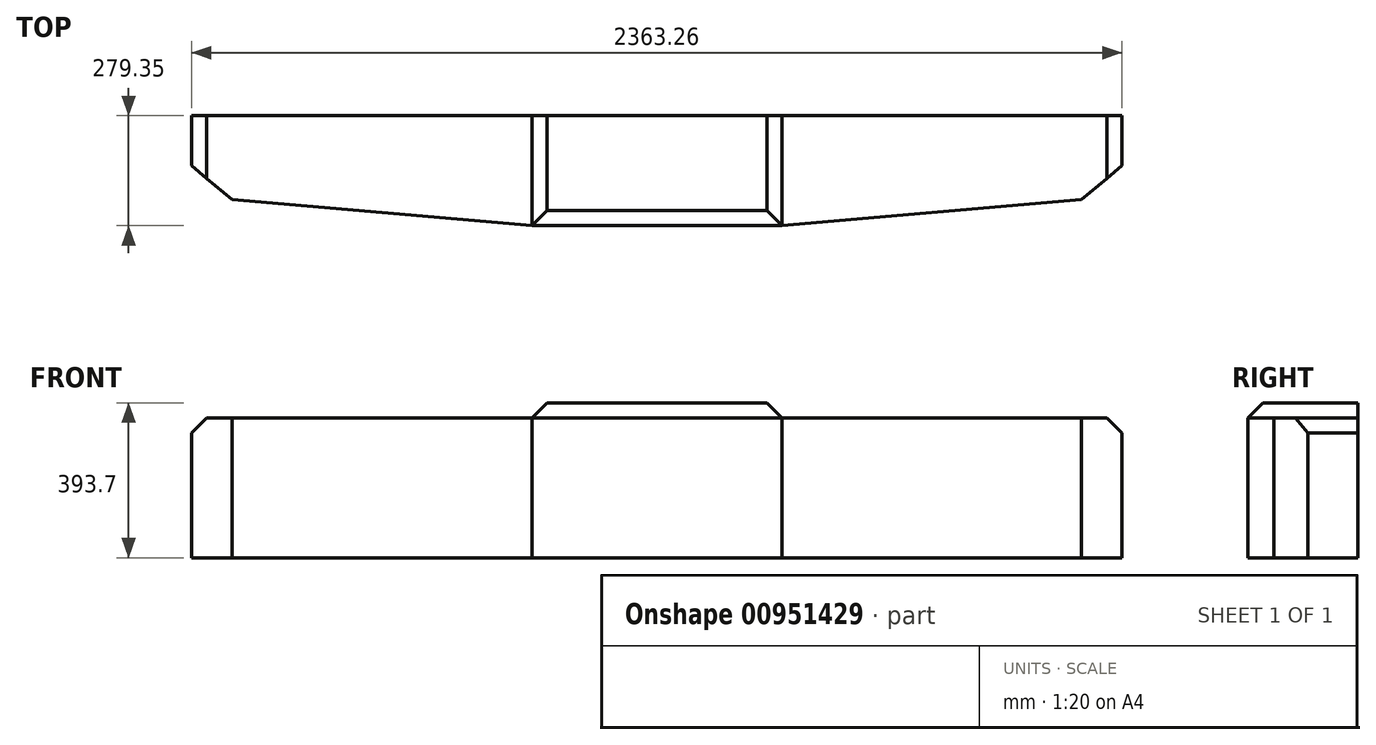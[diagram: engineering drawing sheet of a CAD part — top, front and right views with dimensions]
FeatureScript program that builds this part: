
annotation { "Feature Type Name" : "Feature", "Feature Type Description" : "" }
export const myFeature = defineFeature(function(context is Context, id is Id, definition is map)
    precondition{}
    {
        {
            var Q0;
            Q0=qCreatedBy(makeId("Top.planeOp"),FACE);
            var sketch = newSketch(context, id + "F0", { "sketchPlane" : qUnion([Q0])});
            skLineSegment(sketch, "E0", {"start": v(0, 0) * mm, "end": v(0, -127) * mm});
            skLineSegment(sketch, "E1", {"start": v(0, -127) * mm, "end": v(102.1, -212.68) * mm});
            skLineSegment(sketch, "E2", {"start": v(102.1, -212.68) * mm, "end": v(864.1, -279.35) * mm});
            skLineSegment(sketch, "E3", {"start": v(864.1, -279.35) * mm, "end": v(1499.1, -279.35) * mm});
            skLineSegment(sketch, "E4", {"start": v(1499.1, -279.35) * mm, "end": v(2261.1, -212.71) * mm});
            skLineSegment(sketch, "E5", {"start": v(2261.1, -212.71) * mm, "end": v(2363.26, -127) * mm});
            skLineSegment(sketch, "E6", {"start": v(2363.26, -127) * mm, "end": v(2363.26, 0) * mm});
            skLineSegment(sketch, "E7", {"start": v(2363.26, 0) * mm, "end": v(0, 0) * mm});
            skSolve(sketch);
        }
        {
            var Q0;
            Q0 = qSketchRegion(id + "F0", true);
            extrude(context, id + "F1", {"entities" : qUnion([Q0]), "depth" : 355.6 * mm, "offsetDistance" : 25.4 * mm});
        }
        {
            var Q0;
            Q0=makeQuery(id+"F1.opExtrude","CAP_FACE",FACE,{"disambiguationData":[OSD([sQuery(id+"F0.wireOp",EDGE,"E0"),sQuery(id+"F0.wireOp",EDGE,"E1"),sQuery(id+"F0.wireOp",EDGE,"E2"),sQuery(id+"F0.wireOp",EDGE,"E3"),sQuery(id+"F0.wireOp",EDGE,"E4"),sQuery(id+"F0.wireOp",EDGE,"E5"),sQuery(id+"F0.wireOp",EDGE,"E6"),sQuery(id+"F0.wireOp",EDGE,"E7")])],"isStart":false});
            var sketch = newSketch(context, id + "F2", { "sketchPlane" : qUnion([Q0])});
            skLineSegment(sketch, "E8.bottom", {"start": v(864.1, -279.35) * mm, "end": v(1499.1, -279.35) * mm});
            skLineSegment(sketch, "E8.top", {"start": v(864.1, 0) * mm, "end": v(1499.1, 0) * mm});
            skLineSegment(sketch, "E8.left", {"start": v(864.1, -279.35) * mm, "end": v(864.1, 0) * mm});
            skLineSegment(sketch, "E8.right", {"start": v(1499.1, -279.35) * mm, "end": v(1499.1, 0) * mm});
            skSolve(sketch);
        }
        {
            var Q0;
            Q0 = qSketchRegion(id + "F2", true);
            extrude(context, id + "F3", {"entities" : qUnion([Q0]), "operationType" : NewBodyOperationType.ADD, "depth" : 38.1 * mm, "offsetDistance" : 25.4 * mm});
        }
        {
            var Q0;
            Q0=makeQuery(id+"F3.opExtrude","CAP_EDGE",EDGE,{"disambiguationData":[OSD([sQuery(id+"F2.wireOp",EDGE,"E8.left")])],"isStart":false});
            var Q1;
            Q1=makeQuery(id+"F3.opExtrude","CAP_EDGE",EDGE,{"disambiguationData":[OSD([sQuery(id+"F2.wireOp",EDGE,"E8.right")])],"isStart":false});
            chamfer(context, id + "F4", {"entities" : qUnion([Q0, Q1]), "width" : 38.1 * mm, "tangentPropagation" : true});
        }
        {
            var Q0;
            Q0=makeQuery(id+"F1.opExtrude","CAP_EDGE",EDGE,{"disambiguationData":[OSD([sQuery(id+"F0.wireOp",EDGE,"E0")])],"isStart":false});
            var Q1;
            Q1=makeQuery(id+"F3.opExtrude","CAP_EDGE",EDGE,{"disambiguationData":[OSD([sQuery(id+"F2.wireOp",EDGE,"E8.bottom")])],"isStart":false});
            var Q2;
            Q2=makeQuery(id+"F1.opExtrude","CAP_EDGE",EDGE,{"disambiguationData":[OSD([sQuery(id+"F0.wireOp",EDGE,"E6")])],"isStart":false});
            chamfer(context, id + "F5", {"entities" : qUnion([Q0, Q1, Q2]), "width" : 38.1 * mm, "tangentPropagation" : true});
        }
    });
